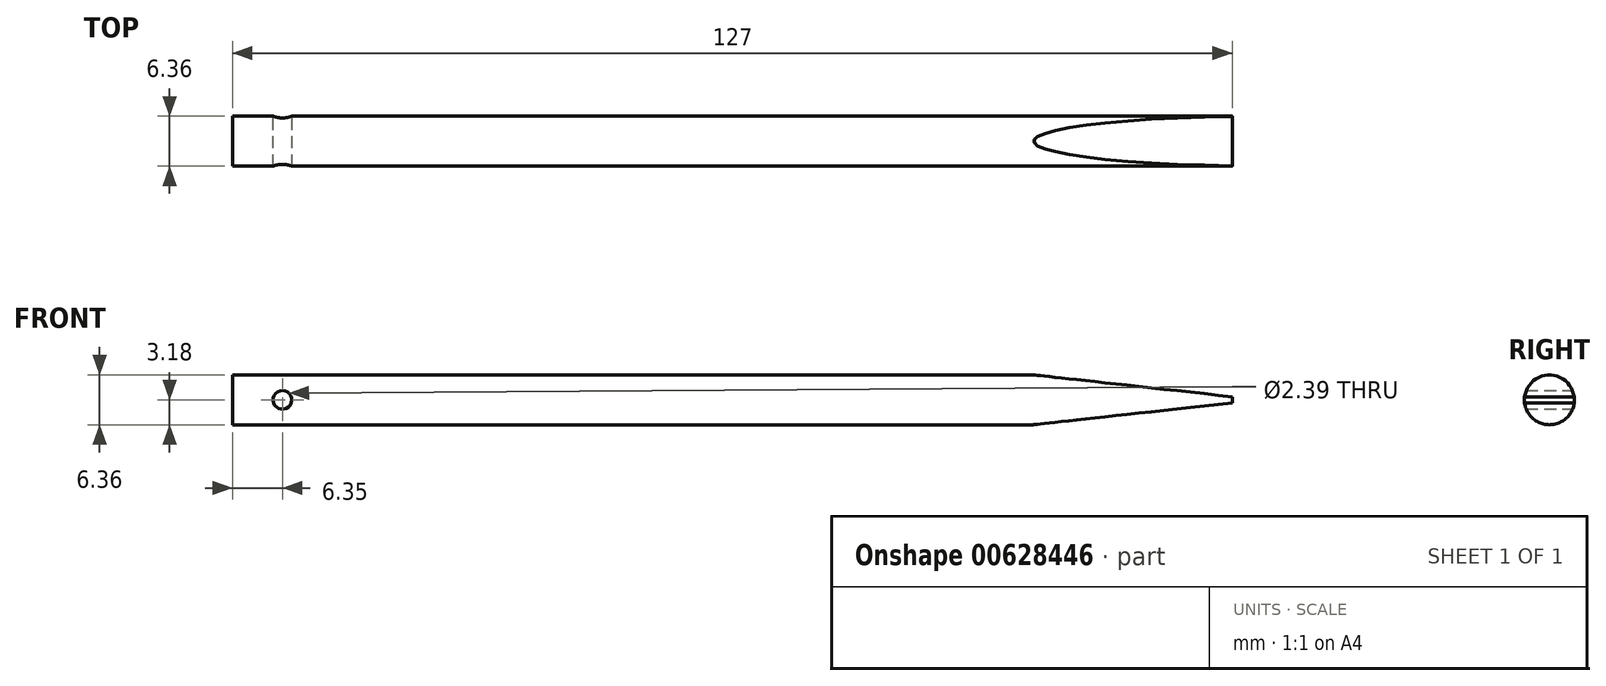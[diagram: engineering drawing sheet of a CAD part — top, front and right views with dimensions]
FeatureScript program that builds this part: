
annotation { "Feature Type Name" : "Feature", "Feature Type Description" : "" }
export const myFeature = defineFeature(function(context is Context, id is Id, definition is map)
    precondition{}
    {
        {
            var Q0;
            Q0=qCreatedBy(makeId("Right.planeOp"),FACE);
            var sketch = newSketch(context, id + "F0", { "sketchPlane" : qUnion([Q0])});
            skCircle(sketch, "E0", {"center": v(0, 0) * mm, "radius": 3.18 * mm});
            skSolve(sketch);
        }
        {
            var Q0;
            Q0 = qSketchRegion(id + "F0", true);
            extrude(context, id + "F1", {"entities" : qUnion([Q0]), "oppositeDirection" : true, "depth" : 127 * mm, "offsetDistance" : 25.4 * mm});
        }
        {
            var Q0;
            Q0=qCreatedBy(makeId("Front.planeOp"),FACE);
            var sketch = newSketch(context, id + "F2", { "sketchPlane" : qUnion([Q0])});
            skCircle(sketch, "E1", {"center": v(-120.65, 0) * mm, "radius": 1.2 * mm});
            skLineSegment(sketch, "E2", {"start": v(0, 0.38) * mm, "end": v(-25.4, 3.19) * mm});
            skLineSegment(sketch, "E3", {"start": v(-25.4, 3.19) * mm, "end": v(-25.4, 4.77) * mm});
            skLineSegment(sketch, "E4", {"start": v(-25.4, 4.77) * mm, "end": v(0, 4.77) * mm});
            skLineSegment(sketch, "E5", {"start": v(0, 4.77) * mm, "end": v(0, 0.38) * mm});
            skLineSegment(sketch, "E6.MirrorCS", {"start": v(0, -0.38) * mm, "end": v(-25.4, -3.19) * mm});
            skLineSegment(sketch, "E7.MirrorCS", {"start": v(-25.4, -4.77) * mm, "end": v(0, -4.77) * mm});
            skLineSegment(sketch, "E8.MirrorCS", {"start": v(0, -4.77) * mm, "end": v(0, -0.38) * mm});
            skLineSegment(sketch, "E9.MirrorCS", {"start": v(-25.4, -3.19) * mm, "end": v(-25.4, -4.77) * mm});
            skSolve(sketch);
        }
        {
            var Q0;
            Q0 = qSketchRegion(id + "F2", true);
            extrude(context, id + "F3", {"entities" : qUnion([Q0]), "operationType" : NewBodyOperationType.REMOVE, "endBound" : BoundingType.SYMMETRIC, "depth" : 25.4 * mm, "offsetDistance" : 25.4 * mm});
        }
    });
